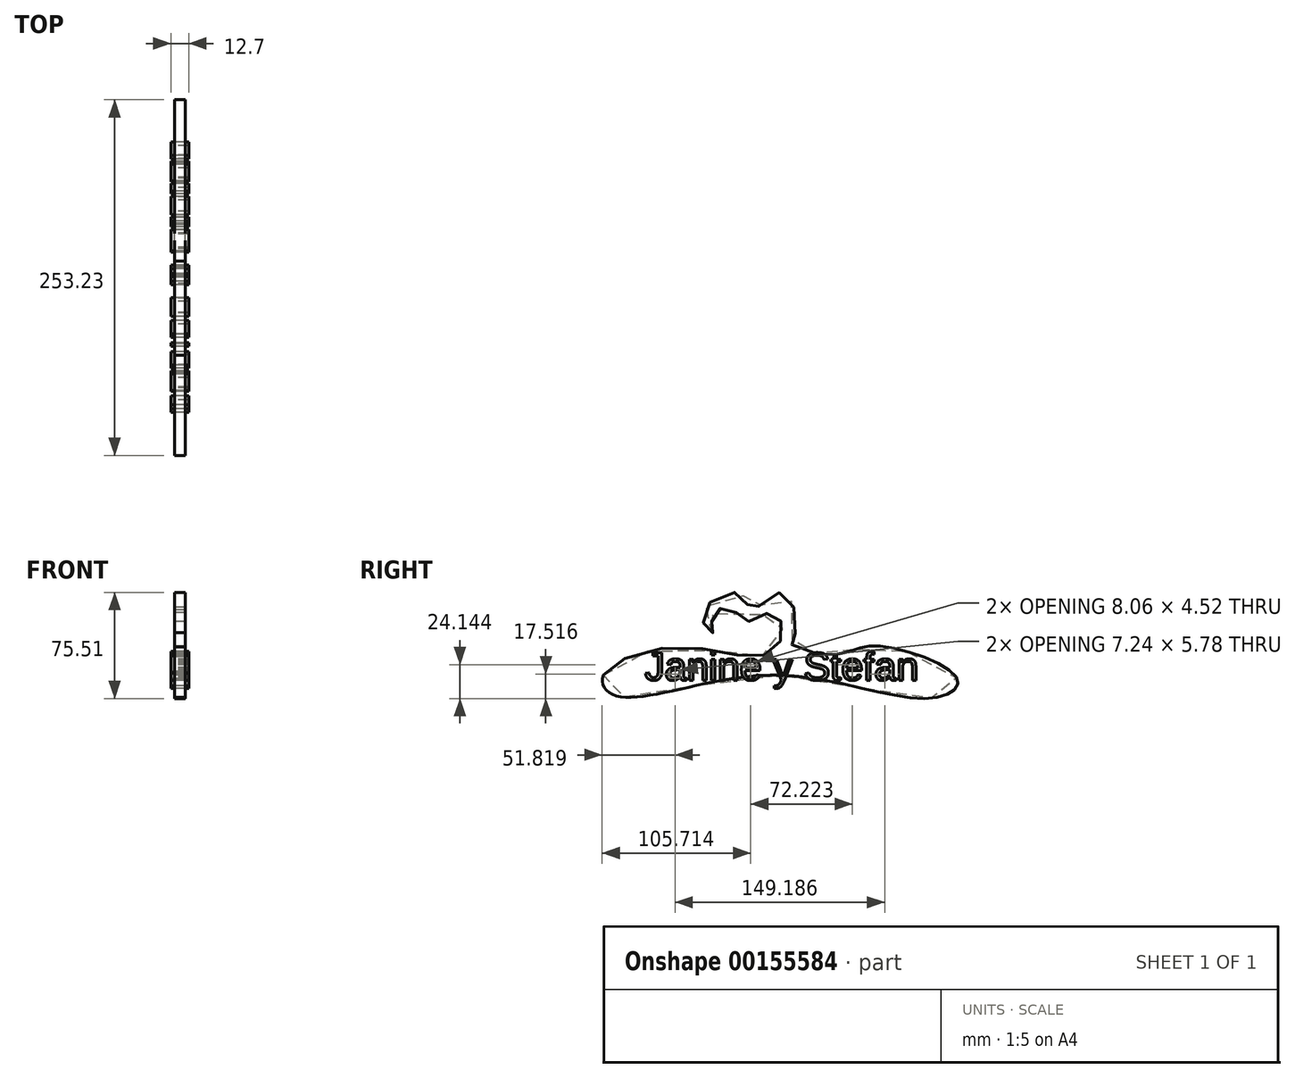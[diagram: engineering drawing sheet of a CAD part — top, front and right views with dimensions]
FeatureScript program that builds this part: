
annotation { "Feature Type Name" : "Feature", "Feature Type Description" : "" }
export const myFeature = defineFeature(function(context is Context, id is Id, definition is map)
    precondition{}
    {
        {
            var Q0;
            Q0=qCreatedBy(makeId("Right.planeOp"),FACE);
            var sketch = newSketch(context, id + "F0", { "sketchPlane" : qUnion([Q0])});
            skText(sketch, "E0", { "text": "Janine y Stefan", "fontName": "Arimo-Regular.ttf"});
            const initialGuessF0  = {"E0": [-0.0895, -0.00353, 1, 0, 0.02034]};
            skSetInitialGuess(sketch, initialGuessF0);
            skSolve(sketch);
        }
        {
            var Q0;
            Q0 = qSketchRegion(id + "F0", true);
            extrude(context, id + "F1", {"entities" : qUnion([Q0]), "endBound" : BoundingType.SYMMETRIC, "depth" : 12.7 * mm});
        }
        {
            var Q0;
            Q0=qCreatedBy(makeId("Right.planeOp"),FACE);
            var sketch = newSketch(context, id + "F2", { "sketchPlane" : qUnion([Q0])});
            skFitSpline(sketch, "E1", {"points": [v(-118.97, 0) * mm, v(-62.01, 20.07) * mm, v(-5.06, 14.1) * mm, v(8.78, 31.73) * mm, v(0, 44.48) * mm, v(-17.26, 38.24) * mm, v(-28.38, 47.73) * mm, v(-41.94, 42.31) * mm, v(-40.32, 31.2) * mm, v(-43.03, 30.65) * mm, v(-47.64, 45.84) * mm, v(-21.06, 57.77) * mm, v(-13.46, 46.38) * mm, v(7.7, 58.85) * mm, v(18, 31.46) * mm, v(14.74, 22.24) * mm, v(46.2, 14.92) * mm, v(74.95, 20.88) * mm, v(133, -2.98) * mm, v(115.1, -16.27) * mm, v(0, 0) * mm, v(-110.02, -14.65) * mm, v(-118.97, 0) * mm]});
            skSolve(sketch);
        }
        {
            var Q0;
            Q0 = qSketchRegion(id + "F2", true);
            extrude(context, id + "F3", {"entities" : qUnion([Q0]), "endBound" : BoundingType.SYMMETRIC, "depth" : 7.62 * mm});
        }
    });
